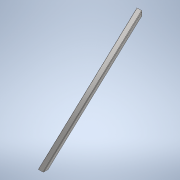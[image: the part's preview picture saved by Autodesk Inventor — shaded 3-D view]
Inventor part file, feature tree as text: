
AUTODESK INVENTOR PART (.ipt)
format: ipt  version: 2021 (Build 250183000, 183)  size: 134,656 bytes
history: native  units: mm
features: plane x2, split x2, sweep x1, fillet x1, other x1, sketch x1
ambient origin geometry x8: Origin, YZ Plane, XZ Plane, XY Plane, X Axis, Y Axis, Z Axis, Center Point
bodies: Solid1 (feature_tree)
feature tree (8):
  sweep  "Sweep1"
  fillet  "Fillet1"  Radius=25.0mm
  plane  "Work Plane2"
  split  "Split2"
  plane  "Work Plane3"
  split  "Split3"
  other  "profile"
  sketch  "3D Sketch1"
